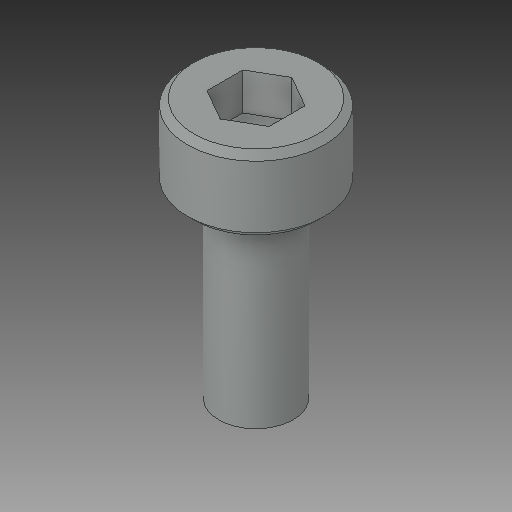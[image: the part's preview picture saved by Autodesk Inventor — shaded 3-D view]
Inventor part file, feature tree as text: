
AUTODESK INVENTOR PART (.ipt)
format: ipt  version: 2018 (Build 220112000, 112)  size: 105,984 bytes
history: native  units: in
note: dims shown in document units (in); Inventor stores cm internally (conversion verified against a paired STEP export)
features: chamfer x1
ambient origin geometry x8: Origin, YZ Plane, XZ Plane, XY Plane, X Axis, Y Axis, Z Axis, Center Point
bodies: Solid1 (feature_tree)
feature tree (1):
  chamfer  "Chamfer2"  [1 undecoded]
note: 1 required parameter value undecoded (feature->parameter linkage not recoverable at this tier; creation-order binding heuristic only, values carry confidence <= 0.55)
